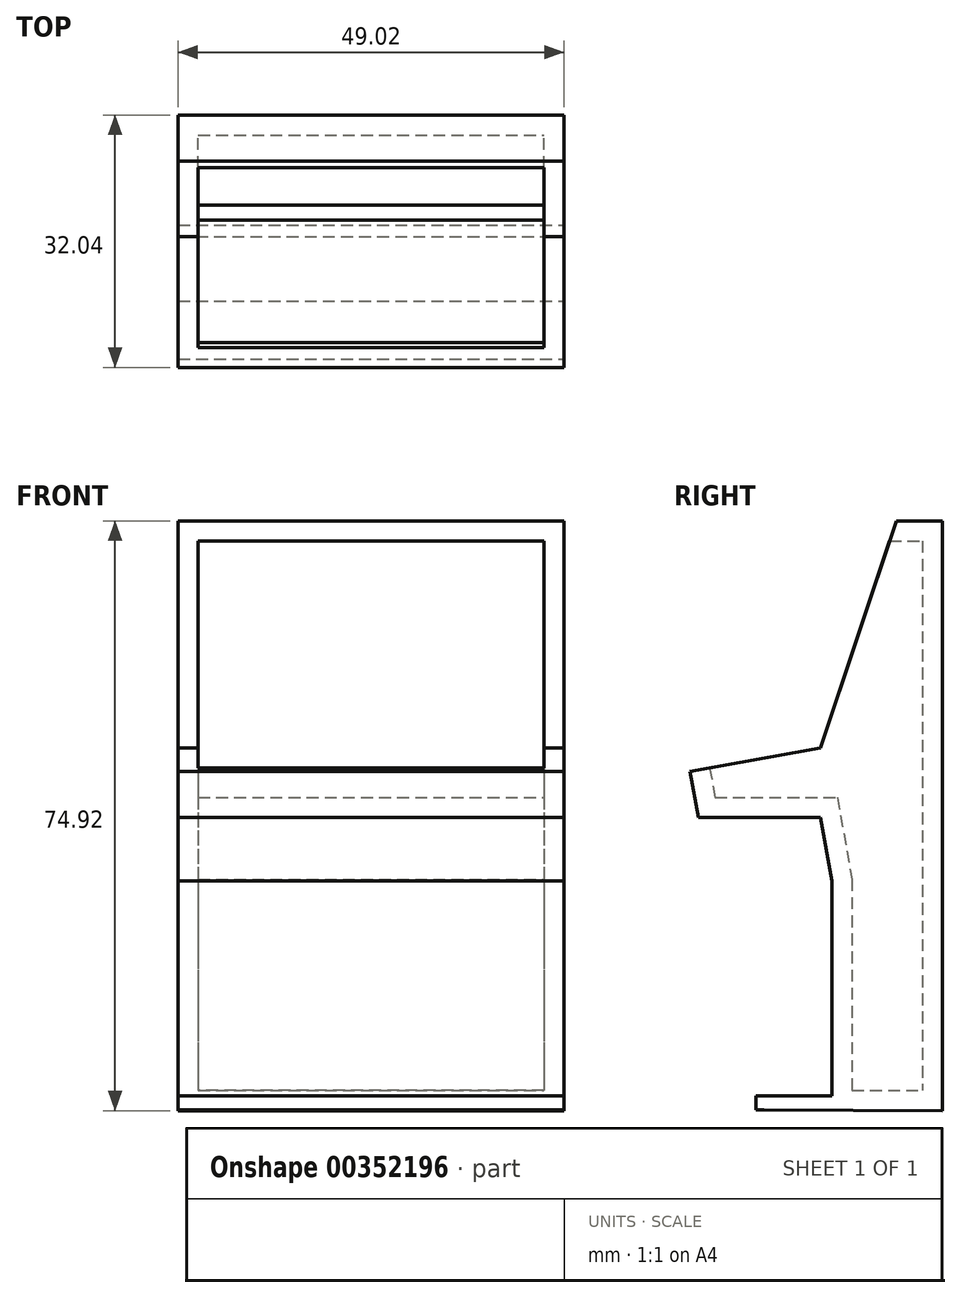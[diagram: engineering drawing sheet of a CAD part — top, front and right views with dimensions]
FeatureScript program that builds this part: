
annotation { "Feature Type Name" : "Feature", "Feature Type Description" : "" }
export const myFeature = defineFeature(function(context is Context, id is Id, definition is map)
    precondition{}
    {
        {
            var Q0;
            Q0=qCreatedBy(makeId("Right.planeOp"),FACE);
            var sketch = newSketch(context, id + "F0", { "sketchPlane" : qUnion([Q0])});
            skLineSegment(sketch, "E0", {"start": v(-15.08, -5.55) * mm, "end": v(1.5, -2.54) * mm});
            skLineSegment(sketch, "E1", {"start": v(1.5, -2.54) * mm, "end": v(11.12, 26.3) * mm});
            skLineSegment(sketch, "E2", {"start": v(11.12, 26.3) * mm, "end": v(16.96, 26.3) * mm});
            skLineSegment(sketch, "E3", {"start": v(16.96, 26.3) * mm, "end": v(16.96, -48.63) * mm});
            skLineSegment(sketch, "E4", {"start": v(-15.08, -5.55) * mm, "end": v(-14.02, -11.4) * mm});
            skLineSegment(sketch, "E5", {"start": v(-14.02, -11.4) * mm, "end": v(1.5, -11.4) * mm});
            skLineSegment(sketch, "E6", {"start": v(1.5, -11.4) * mm, "end": v(2.97, -19.45) * mm});
            skLineSegment(sketch, "E7", {"start": v(2.97, -19.45) * mm, "end": v(2.97, -46.74) * mm});
            skLineSegment(sketch, "E8", {"start": v(2.97, -46.74) * mm, "end": v(-5.7, -46.74) * mm});
            skLineSegment(sketch, "E9", {"start": v(-5.7, -46.74) * mm, "end": v(-5.69, -48.53) * mm});
            skLineSegment(sketch, "E10", {"start": v(-5.69, -48.53) * mm, "end": v(16.96, -48.63) * mm});
            skSolve(sketch);
        }
        {
            var Q0;
            Q0=makeQuery(id+"F0.imprint","IMPRINT",FACE,{"disambiguationData":[TD([[makeQuery(id+"F0.imprint","IMPRINT",EDGE,{"derivedFrom":sQuery(id+"F0.wireOp",EDGE,"E0")}),-1.0]])]});
            extrude(context, id + "F1", {"entities" : qUnion([Q0]), "oppositeDirection" : true, "depth" : 49.02 * mm});
        }
        {
            var Q0;
            Q0=makeQuery(id+"F1.opExtrude","SWEPT_FACE",FACE,{"disambiguationData":[OSD([sQuery(id+"F0.wireOp",EDGE,"E1")])]});
            var Q1;
            Q1=makeQuery(id+"F1.opExtrude","SWEPT_FACE",FACE,{"disambiguationData":[OSD([sQuery(id+"F0.wireOp",EDGE,"E0")])]});
            shell(context, id + "F2", {"entities" : qUnion([Q0, Q1]), "thickness" : 2.54 * mm});
        }
        {
            var Q0;
            Q0=makeQuery(id+"F1.opExtrude","SWEPT_FACE",FACE,{"disambiguationData":[OSD([sQuery(id+"F0.wireOp",EDGE,"E0")])]});
            var sketch = newSketch(context, id + "F3", { "sketchPlane" : qUnion([Q0])});
            skLineSegment(sketch, "E11.bottom", {"start": v(-2.54, -13.29) * mm, "end": v(-46.48, -13.29) * mm});
            skLineSegment(sketch, "E11.top", {"start": v(-2.54, -13.29) * mm, "end": v(-46.48, -13.29) * mm});
            skLineSegment(sketch, "E11.left", {"start": v(-2.54, -13.29) * mm, "end": v(-2.54, -13.29) * mm});
            skLineSegment(sketch, "E11.right", {"start": v(-46.48, -13.29) * mm, "end": v(-46.48, -13.29) * mm});
            skLineSegment(sketch, "E12.bottom", {"start": v(-46.48, -13.29) * mm, "end": v(-2.54, -13.29) * mm});
            skLineSegment(sketch, "E12.top", {"start": v(-46.48, 1.03) * mm, "end": v(-2.54, 1.03) * mm});
            skLineSegment(sketch, "E12.left", {"start": v(-46.48, -13.29) * mm, "end": v(-46.48, 1.03) * mm});
            skLineSegment(sketch, "E12.right", {"start": v(-2.54, -13.29) * mm, "end": v(-2.54, 1.03) * mm});
            skSolve(sketch);
        }
        {
            var Q0;
            Q0=makeQuery(id+"F1.opExtrude","SWEPT_FACE",FACE,{"disambiguationData":[OSD([sQuery(id+"F0.wireOp",EDGE,"E7"),sQuery(id+"F0.wireOp",EDGE,"t7V8kqDJ-uGgu-wJj0-Ik0c-o4IvpzlLW7QX"),sQuery(id+"F0.wireOp",EDGE,"ebeXymbc-pTHe-Bqyb-jlUC-bMZQNnTWN57G")])]});
            var sketch = newSketch(context, id + "F4", { "sketchPlane" : qUnion([Q0])});
            skLineSegment(sketch, "E13", {"start": v(-49.02, -48.53) * mm, "end": v(0, -48.53) * mm});
            skLineSegment(sketch, "E14", {"start": v(0, -48.53) * mm, "end": v(0, -43.28) * mm});
            skLineSegment(sketch, "E15", {"start": v(0, -43.28) * mm, "end": v(-49.02, -43.28) * mm});
            skLineSegment(sketch, "E16", {"start": v(-49.02, -43.28) * mm, "end": v(-49.02, -48.53) * mm});
            skLineSegment(sketch, "E17", {"start": v(-49.02, -48.53) * mm, "end": v(-49.02, -43.28) * mm});
            skSolve(sketch);
        }
        {
            var Q0;
            Q0=makeQuery(id+"F4.imprint","IMPRINT",FACE,{"disambiguationData":[TD([[makeQuery(id+"F4.imprint","IMPRINT",EDGE,{"derivedFrom":sQuery(id+"F4.wireOp",EDGE,"E13")}),1.0]])]});
            extrude(context, id + "F5", {"entities" : qUnion([Q0]), "operationType" : NewBodyOperationType.ADD, "depth" : 9.65 * mm});
        }
        {
            var Q0;
            Q0=makeQuery(id+"F1.opExtrude","SWEPT_FACE",FACE,{"disambiguationData":[OSD([sQuery(id+"F0.wireOp",EDGE,"E3"),sQuery(id+"F0.wireOp",EDGE,"GDaOwqO8-DlV2-066S-Q4eb-zltXCY0JFRe5")])]});
            var sketch = newSketch(context, id + "F6", { "sketchPlane" : qUnion([Q0])});
            skLineSegment(sketch, "E18.bottom", {"start": v(10.18, 22.09) * mm, "end": v(39.08, 22.09) * mm});
            skLineSegment(sketch, "E18.top", {"start": v(10.18, -43.8) * mm, "end": v(39.08, -43.8) * mm});
            skLineSegment(sketch, "E18.left", {"start": v(3.83, 15.74) * mm, "end": v(3.83, -37.46) * mm});
            skLineSegment(sketch, "E18.right", {"start": v(45.43, 15.74) * mm, "end": v(45.43, -37.46) * mm});
            skPoint(sketch, "E19.visualSharp", {"position": v(3.83, 22.09) * mm});
            skArc(sketch, "E19.filletArc", {"start": v(10.18, 22.09) * mm, "mid": v(5.7, 20.23) * mm, "end": v(3.83, 15.74) * mm});
            skPoint(sketch, "E20.visualSharp", {"position": v(45.43, 22.09) * mm});
            skArc(sketch, "E20.filletArc", {"start": v(45.43, 15.74) * mm, "mid": v(43.57, 20.23) * mm, "end": v(39.08, 22.09) * mm});
            skPoint(sketch, "E21.visualSharp", {"position": v(3.83, -43.8) * mm});
            skArc(sketch, "E21.filletArc", {"start": v(3.83, -37.46) * mm, "mid": v(5.7, -41.95) * mm, "end": v(10.18, -43.8) * mm});
            skPoint(sketch, "E22.visualSharp", {"position": v(45.43, -43.8) * mm});
            skArc(sketch, "E22.filletArc", {"start": v(39.08, -43.8) * mm, "mid": v(43.57, -41.95) * mm, "end": v(45.43, -37.46) * mm});
            skSolve(sketch);
        }
        {
            var Q0;
            Q0=makeQuery(id+"F1.opExtrude","SWEPT_FACE",FACE,{"disambiguationData":[OSD([sQuery(id+"F0.wireOp",EDGE,"E1")])]});
            var sketch = newSketch(context, id + "F7", { "sketchPlane" : qUnion([Q0])});
            skLineSegment(sketch, "E23.bottom", {"start": v(-46.48, -1.93) * mm, "end": v(-2.54, -1.93) * mm});
            skLineSegment(sketch, "E23.top", {"start": v(-46.48, 0.62) * mm, "end": v(-2.54, 0.62) * mm});
            skLineSegment(sketch, "E23.left", {"start": v(-46.48, -1.93) * mm, "end": v(-46.48, 0.62) * mm});
            skLineSegment(sketch, "E23.right", {"start": v(-2.54, -1.93) * mm, "end": v(-2.54, 0.62) * mm});
            skSolve(sketch);
        }
        {
            var Q0;
            Q0=makeQuery(id+"F1.opExtrude","SWEPT_BODY",BODY,{"disambiguationData":[OSD([sQuery(id+"F0.wireOp",EDGE,"E0"),sQuery(id+"F0.wireOp",EDGE,"E1"),sQuery(id+"F0.wireOp",EDGE,"E2"),sQuery(id+"F0.wireOp",EDGE,"E3"),sQuery(id+"F0.wireOp",EDGE,"E4"),sQuery(id+"F0.wireOp",EDGE,"E5"),sQuery(id+"F0.wireOp",EDGE,"E6"),sQuery(id+"F0.wireOp",EDGE,"E7"),sQuery(id+"F0.wireOp",EDGE,"t7V8kqDJ-uGgu-wJj0-Ik0c-o4IvpzlLW7QX"),sQuery(id+"F0.wireOp",EDGE,"ebeXymbc-pTHe-Bqyb-jlUC-bMZQNnTWN57G"),sQuery(id+"F0.wireOp",EDGE,"GDaOwqO8-DlV2-066S-Q4eb-zltXCY0JFRe5"),sQuery(id+"F0.wireOp",EDGE,"FTaeJzFL-QiV6-1QZg-l3Di-SDgnJijt2cH2")])]});
            transform(context, id + "F8", {"entities" : qUnion([Q0]), "transformType" : TransformType.TRANSLATION_3D, "dx" : 0 * mm, "dy" : 0 * mm, "dz" : 0 * mm, "makeCopy" : true});
        }
        {
            var Q0;
            Q0=makeQuery(id+"F8.opPattern","COPY",BODY,{"derivedFrom":makeQuery(id+"F1.opExtrude","SWEPT_BODY",BODY,{"disambiguationData":[OSD([sQuery(id+"F0.wireOp",EDGE,"E0"),sQuery(id+"F0.wireOp",EDGE,"E1"),sQuery(id+"F0.wireOp",EDGE,"E2"),sQuery(id+"F0.wireOp",EDGE,"E3"),sQuery(id+"F0.wireOp",EDGE,"E4"),sQuery(id+"F0.wireOp",EDGE,"E5"),sQuery(id+"F0.wireOp",EDGE,"E6"),sQuery(id+"F0.wireOp",EDGE,"E7"),sQuery(id+"F0.wireOp",EDGE,"t7V8kqDJ-uGgu-wJj0-Ik0c-o4IvpzlLW7QX"),sQuery(id+"F0.wireOp",EDGE,"ebeXymbc-pTHe-Bqyb-jlUC-bMZQNnTWN57G"),sQuery(id+"F0.wireOp",EDGE,"GDaOwqO8-DlV2-066S-Q4eb-zltXCY0JFRe5"),sQuery(id+"F0.wireOp",EDGE,"FTaeJzFL-QiV6-1QZg-l3Di-SDgnJijt2cH2")])]}),"instanceName":"1"});
            deleteBodies(context, id + "F9", {"entities" : qUnion([Q0])});
        }
    });
